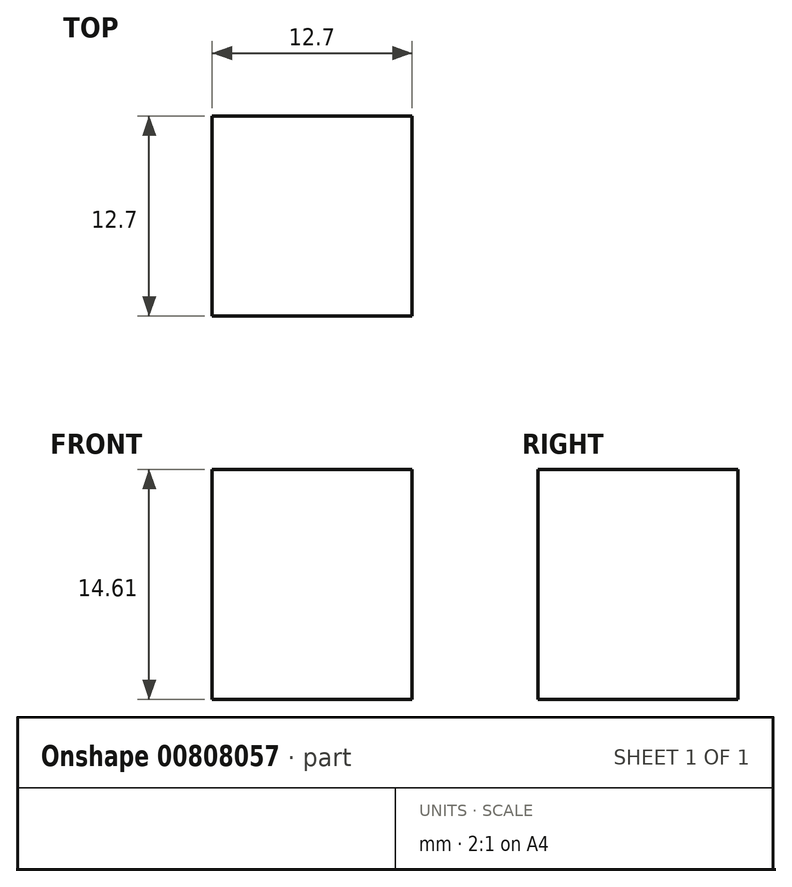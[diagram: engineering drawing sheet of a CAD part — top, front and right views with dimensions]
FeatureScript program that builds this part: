
annotation { "Feature Type Name" : "Feature", "Feature Type Description" : "" }
export const myFeature = defineFeature(function(context is Context, id is Id, definition is map)
    precondition{}
    {
        {
            var Q0;
            Q0=qCreatedBy(makeId("Top.planeOp"),FACE);
            var sketch = newSketch(context, id + "F0", { "sketchPlane" : qUnion([Q0])});
            skLineSegment(sketch, "E0.bottom", {"start": v(0, 0) * mm, "end": v(25.4, 0) * mm});
            skLineSegment(sketch, "E0.top", {"start": v(0, 25.4) * mm, "end": v(25.4, 25.4) * mm});
            skLineSegment(sketch, "E0.left", {"start": v(0, 0) * mm, "end": v(0, 25.4) * mm});
            skLineSegment(sketch, "E0.right", {"start": v(25.4, 0) * mm, "end": v(25.4, 25.4) * mm});
            skSolve(sketch);
        }
        {
            var Q0;
            Q0=makeQuery(id+"F0.imprint","IMPRINT",FACE,{"disambiguationData":[TD([[makeQuery(id+"F0.imprint","IMPRINT",EDGE,{"derivedFrom":sQuery(id+"F0.wireOp",EDGE,"E0.bottom")}),1.0]])]});
            extrude(context, id + "F1", {"entities" : qUnion([Q0]), "depth" : 29.2 * mm, "offsetDistance" : 25.4 * mm});
        }
        {
            var Q0;
            Q0=makeQuery(id+"F1.opExtrude","SWEPT_BODY",BODY,{"disambiguationData":[OSD([sQuery(id+"F0.wireOp",EDGE,"E0.bottom"),sQuery(id+"F0.wireOp",EDGE,"E0.top"),sQuery(id+"F0.wireOp",EDGE,"E0.left"),sQuery(id+"F0.wireOp",EDGE,"E0.right")])]});
            var Q1;
            Q1=qCreatedBy(makeId("Origin.pointOp"),VERTEX);
            transform(context, id + "F2", {"entities" : qUnion([Q0]), "transformType" : TransformType.SCALE_UNIFORMLY, "scale" : .5, "scalePoint" : qUnion([Q1]), "makeCopy" : false});
        }
    });
